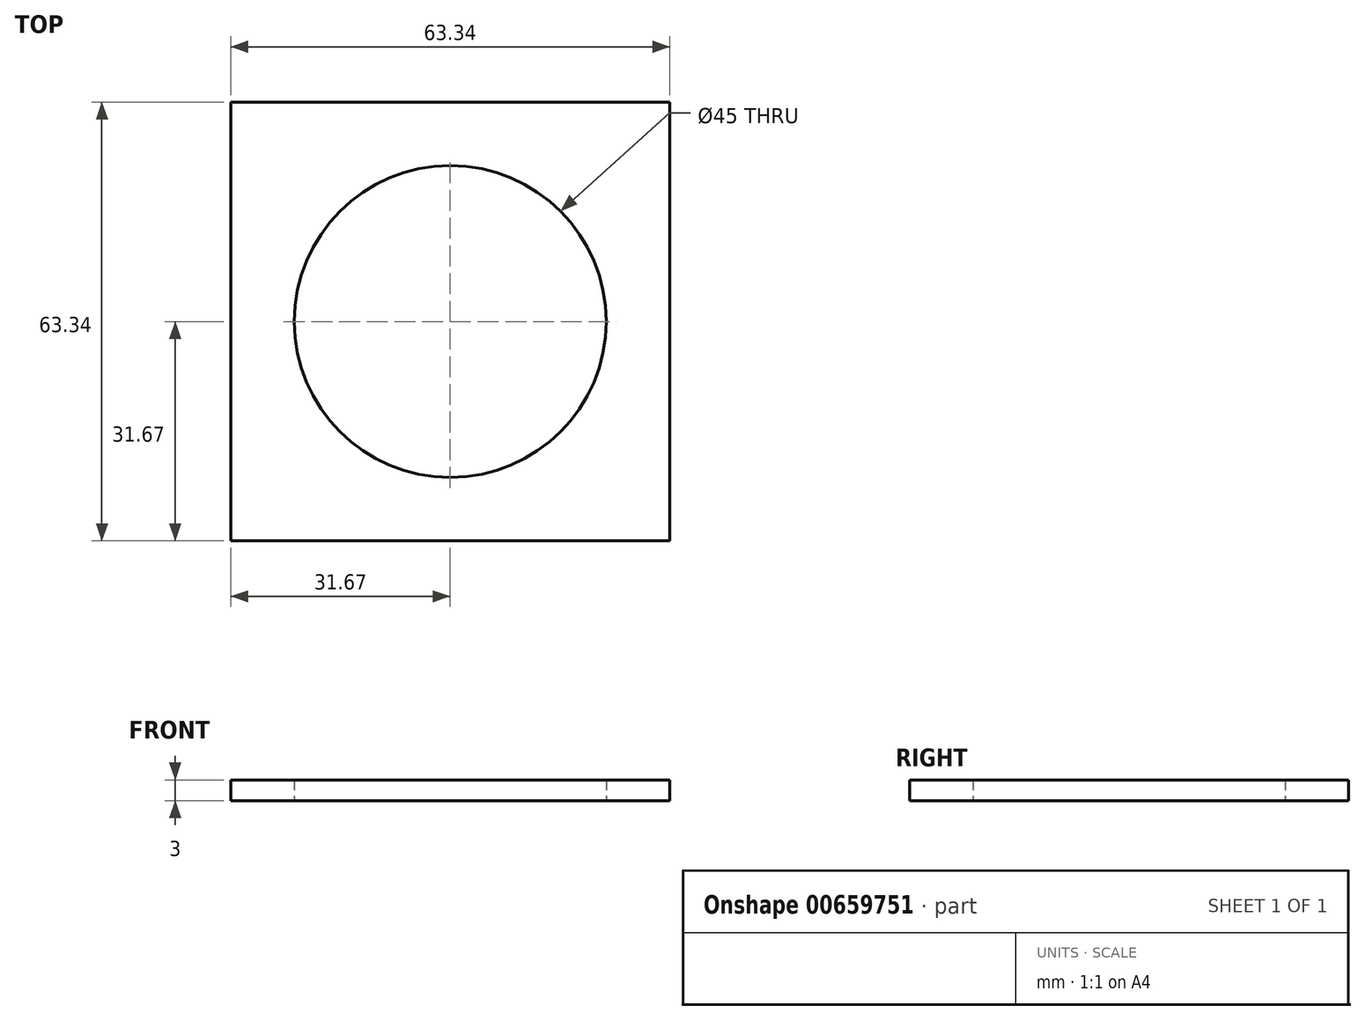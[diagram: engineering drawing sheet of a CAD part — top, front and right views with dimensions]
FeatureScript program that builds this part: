
annotation { "Feature Type Name" : "Feature", "Feature Type Description" : "" }
export const myFeature = defineFeature(function(context is Context, id is Id, definition is map)
    precondition{}
    {
        {
            var Q0;
            Q0=qCreatedBy(makeId("Top.planeOp"),FACE);
            var sketch = newSketch(context, id + "F0", { "sketchPlane" : qUnion([Q0])});
            skLineSegment(sketch, "E0.bottom", {"start": v(-31.67, 31.67) * mm, "end": v(31.67, 31.67) * mm});
            skLineSegment(sketch, "E0.top", {"start": v(-31.67, -31.67) * mm, "end": v(31.67, -31.67) * mm});
            skLineSegment(sketch, "E0.left", {"start": v(-31.67, 31.67) * mm, "end": v(-31.67, -31.67) * mm});
            skLineSegment(sketch, "E0.right", {"start": v(31.67, 31.67) * mm, "end": v(31.67, -31.67) * mm});
            skPoint(sketch, "E0.middle", {"position": v(0, 0) * mm});
            skCircle(sketch, "E1", {"center": v(0, 0) * mm, "radius": 22.5 * mm});
            skSolve(sketch);
        }
        {
            var Q0;
            Q0=makeQuery(id+"F0.imprint","IMPRINT",FACE,{"disambiguationData":[TD([[makeQuery(id+"F0.imprint","IMPRINT",EDGE,{"derivedFrom":sQuery(id+"F0.wireOp",EDGE,"E0.bottom")}),-1.0]])]});
            extrude(context, id + "F1", {"entities" : qUnion([Q0]), "depth" : 3 * mm, "offsetDistance" : 25 * mm});
        }
    });
